# Revit family: IS_CerathermT100_A5813_BIM_NL
name_source: partatom
category: Plumbing Fixtures
units: mm (PartAtom-declared; Revit-internal decimal feet)

## family parameters
Always vertical = No
Cut with Voids When Loaded = No
Part Type = Normal
Room Calculation Point = No
Round Connector Dimension = Use Diameter
Shared = No
Work Plane-Based = No

## types (5) — shared parameters
Accesoires = https://www.idealstandard.nl
Accessories = https://www.idealstandard.nl
Afmetingen = 163 x 79 x 163 mm
AfstandsEenheid = Millimeter
AreaUnits = Millimetres
Artikelomschrijving = CERATHERM T100 THERMOSTATISCHE DUSCHE EINBAUSATZ2/EASY-BUILT
Artikelreferentie = CERATHERM T100 THERMOSTATIC SHOWER BUILT-IN KIT2/EASY-BUILT
Auteur = Ideal Standard
BIMObjectName = IS_IdealStandard_Showermixers_CerathermT100_A5813
BIMobject category = Sanitary
BIMobject category code = Taps & Mixers
BIMobject main category = Sanitary
Bedieningkraan = Handbuch
Bedieningkraanwerk = drehen wissen
Beschrijvingdouchekop = Regenbrause
Beschrijvinggarantie = Herstellergarantie
BimObjectNaam = IS_IdealStandard_Showermixers_CerathermT100_A5813
Brand = Ideal Standard
Brand url = http://www.idealstandard.nl
Breedte = 163.064133
ConnectionType = Installation
CurrencyUnit = €
CurrentRevision = 1
Date of publishing = 24/07/2021
Diepte = 79 mm
Douchebak = No
DurationUnit = Years
Edition number = 1
FaucetFunction = Mixer
FaucetOperation = Turning Knobs Controless
FaucetType = Thermostatic Mixer
Functieindoucheruimte = Thermostat-Brausemischer
Functiekraanwerk = Thermostat-Brausemischer
Garantieonderdelen = 5
Garantieunits = Jaren
GemaaktOp = 27/07/2021
HasIntegralShutOffDevice = No
Help = https://www.idealstandard.nl
Hoogte = 163.04366094306
Hulp = https://www.idealstandard.nl
IFC Classification = Sanitary Terminal
IfcExportAs = IfcValveType
IfcExportType = MIXING
Installatieinstructies = https://www.idealstandard.nl
Installation instructions = https://www.idealstandard.nl
InstallationInstructions = https://www.idealstandard.nl
IsBuiltIn = No
IsHighPressure = No
Klepmechanisme = Drehknöpfe Controlless
LinearUnits = Millimetres
MaintenanceInformation = https://www.idealstandard.nl
Manufacturer = Ideal Standard
Manufacturer name = Ideal Standard
ManufacturerURL = https://www.idealstandard.nl
Materiaal = Messing
Material = Brass
Material main = Brass
Merk = Ideal Standard
ModelReference = CERATHERM T100 THERMOSTATIC SHOWER BUILT-IN KIT2/EASY-BUILT
Montageinstuctie = https://www.idealstandard.nl
NBS Reference Code = 45-35-70/335
NBS Reference Description = Shower mixers
Name = Showermixers_CerathermT100_A5813_IdealStandard
NominalDepth = 79 mm
NominalHeight = 163 mm
NominalLength = 79 mm
NominalWidth = 163 mm
Normen = Showermixers_CerathermT100_A5813_IdealStandard
OppervlakteEenheid = Millimeter
Product Guid = dd48a634-7318-4c33-bef6-f35489df5951
Product SKU = A5813
Product certification = https://www.idealstandard.nl
Product data url = https://bimobject.com
Product family = Sanitary
Product group = Showers
Product name = CERATHERM T100 THERMOSTATIC SHOWER BUILT-IN KIT2/EASY-BUILT
Product url = https://www.idealstandard.nl
ProductInformation = https://www.idealstandard.nl
ProductSoort = Sanitary
Productinformatie = https://www.idealstandard.nl
QR code = http://bimobject.com
Referentie = CERATHERM T100 THERMOSTATIC SHOWER BUILT-IN KIT2/EASY-BUILT
Revisie = 1
Shape = Cylindrical
ShowerType = Thermostatic Shower Mixer
Size = 163 x 79 x 163 mm
Space = Internal
SpareParts = https://www.idealstandard.nl
Technical description = https://www.idealstandard.nl
Telefoonnummer = 077 355 08 08
TestPressure = 10 Bar
Testdruk = 10 Bar
Typeconnectie = Installation
URL = https://www.idealstandard.nl
Uniclass 2.0 Code = PR-35-06-82
Uniclass 2.0 Description = Shower Mixer
Uniclass 2015 Code = Pr_40_20_87_80
Uniclass 2015 Name = Shower thermostatic valves
Uniclass2015Beschrijving = Shower thermostatic valves
Uniclass2015Code = Pr_40_20_87_80
Uniclass2015Referentie = Pr_40_20_87_80
Uniclass2015Title = Shower thermostatic valves
Uniclass2015Version = v1.22
Urlproducent = https://www.idealstandard.nl
ValutaEenheid = Euro
Versie = 1
Version = 1
VolumeUnits = Litres
Volumeunits = Liters
Vorm = zylindrisch
WRASURL = https://www.wrasapprovals.co.uk
WarrantyDescription = Manufacturer warranty
WarrantyDurationUnit = Years
Wisselstukken = https://www.idealstandard.nl
Youtube clip = https://www.youtube.com
zero-valued in all types: BrutoGewicht, Cost, Lengte, Vervangingskosten

## per-type parameters (varying)
| type | Afwerking | Artikelnummer | BarCode | Barcode | Color | Description | Eigenschappen | Features | Finish | GTIN code | Kleur | MainColor | Model | ModelNumber | NettWeight | Nettogewicht |
| A5813AA - CERATHERM T100 THERMOSTATIC SHOWER BUILT-IN KIT2/EASY-BUILT  - CHROME | Chrom | A5813AA | 4015413350242 | 4015413350242 | Chrom | CERATHERM T100 THERMOSTATISCHE DUSCHE EINBAUSATZ2/EASY-BUILT - CHROM | THERMOSTATISCHE DUSCHE EINBAUSATZ2/EASY-BUILT - CHROM | THERMOSTATISCHE DUSCHE EINBAUSATZ2/EASY-BUILT - CHROM | Chrom | https://4015413350242 | Chrom | Chrom | A5813AA | A5813AA | 1.6 | 1.6 |
| A5813A5 - CERATHERM T100 THERMOSTATIC SHOWER BUILT-IN KIT2/EASY-BUILT  - MAGNETIC GREY | magnetisch grau | A5813A5 | 4015413350259 | 4015413350259 | magnetisch grau | CERATHERM T100 THERMOSTATISCHE DUSCHE EINBAUSATZ2/EASY-BUILT - MAGNETISCHES GRAU | THERMOSTATISCHE DUSCHE EINBAUSATZ2/EASY-BUILT - MAGNETISCHES GRAU | THERMOSTATISCHE DUSCHE EINBAUSATZ2/EASY-BUILT - MAGNETISCHES GRAU | magnetisch grau | https://4015413350259 | magnetisch grau | magnetisch grau | A5813A5 | A5813A5 | 1.77 | 1.77 |
| A5813XG - CERATHERM T100 THERMOSTATIC SHOWER BUILT-IN KIT2/EASY-BUILT  - SILK BLACK | Seide schwarz | A5813XG | 4015413350587 | 4015413350587 | Seide schwarz | CERATHERM T100 THERMOSTATISCHE DUSCHE EINBAUSATZ2/EASY-BUILT - SEIDE SCHWARZ | THERMOSTATISCHE DUSCHE EINBAUSATZ2/EASY-BUILT - SEIDE SCHWARZ | THERMOSTATISCHE DUSCHE EINBAUSATZ2/EASY-BUILT - SEIDE SCHWARZ | Seide schwarz | https://4015413350587 | Seide schwarz | Seide schwarz | A5813XG | A5813XG | 1.6 | 1.6 |
| A5813GN - CERATHERM T100 THERMOSTATIC SHOWER BUILT-IN KIT2/EASY-BUILT  - SILVER STORM | silberner Sturm | A5813GN | 4015413350235 | 4015413350235 | silberner Sturm | CERATHERM T100 THERMOSTATISCHE DUSCHE EINBAUSATZ2/EASY-BUILT - SILBER STURM | THERMOSTATISCHE DUSCHE EINBAUSATZ2/EASY-BUILT - SILBER STURM | THERMOSTATISCHE DUSCHE EINBAUSATZ2/EASY-BUILT - SILBER STURM | silberner Sturm | https://4015413350235 | silberner Sturm | silberner Sturm | A5813GN | A5813GN | 1.78 | 1.78 |
| A5813A2 - CERATHERM T100 THERMOSTATIC SHOWER BUILT-IN KIT2/EASY-BUILT  - BRUSH GOLD | Pinsel gold | A5813A2 | 4015413350266 | 4015413350266 | Pinsel gold | CERATHERM T100 THERMOSTATISCHE DUSCHE EINBAUSATZ2/EASY-BUILT - PINSEL GOLD | THERMOSTATISCHE DUSCHE EINBAUSATZ2/EASY-BUILT - PINSEL GOLD | THERMOSTATISCHE DUSCHE EINBAUSATZ2/EASY-BUILT - PINSEL GOLD | Pinsel gold | https://4015413350266 | Pinsel gold | Pinsel gold | A5813A2 | A5813A2 | 1.77 | 1.77 |

## geometry (parser evidence)
native form markers: Sweep x1
no freeform markers — native parametric forms only
